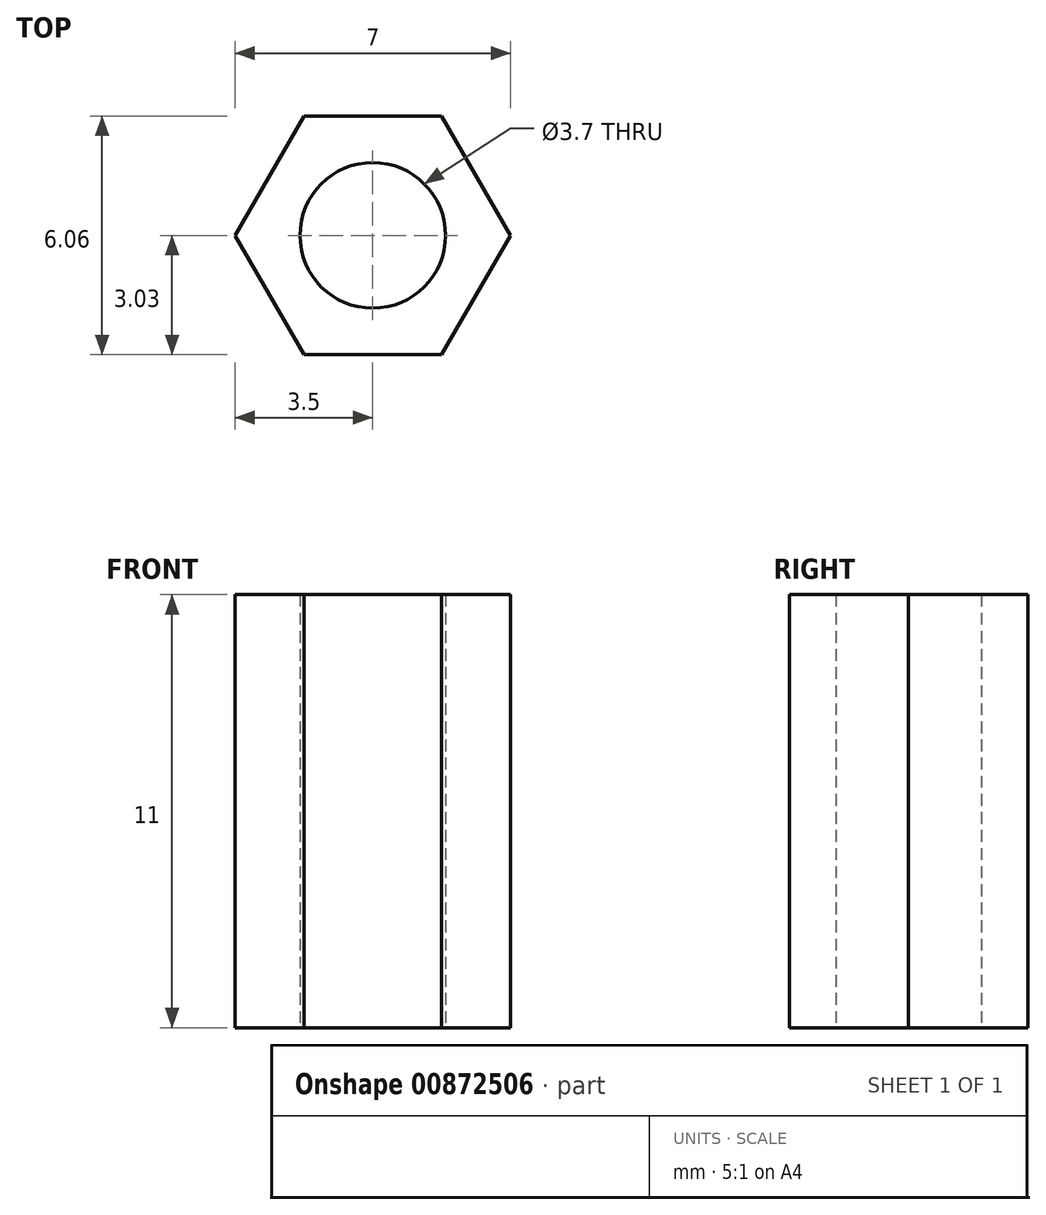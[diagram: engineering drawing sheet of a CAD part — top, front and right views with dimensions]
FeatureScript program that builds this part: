
annotation { "Feature Type Name" : "Feature", "Feature Type Description" : "" }
export const myFeature = defineFeature(function(context is Context, id is Id, definition is map)
    precondition{}
    {
        {
            var Q0;
            Q0=qCreatedBy(makeId("Top.planeOp"),FACE);
            var sketch = newSketch(context, id + "F0", { "sketchPlane" : qUnion([Q0])});
            skCircle(sketch, "E0", {"center": v(0, 0) * mm, "radius": 1.85 * mm});
            skCircle(sketch, "E1.cCircle", {"center": v(0, 0) * mm, "radius": 3.5 * mm, "construction": true});
            skLineSegment(sketch, "E1.0", {"start": v(3.5, 0) * mm, "end": v(1.75, -3.03) * mm});
            skLineSegment(sketch, "E1.1", {"start": v(1.75, -3.03) * mm, "end": v(-1.75, -3.03) * mm});
            skLineSegment(sketch, "E1.2", {"start": v(-1.75, -3.03) * mm, "end": v(-3.5, 0) * mm});
            skLineSegment(sketch, "E1.3", {"start": v(-3.5, 0) * mm, "end": v(-1.75, 3.03) * mm});
            skLineSegment(sketch, "E1.4", {"start": v(-1.75, 3.03) * mm, "end": v(1.75, 3.03) * mm});
            skLineSegment(sketch, "E1.5", {"start": v(1.75, 3.03) * mm, "end": v(3.5, 0) * mm});
            skSolve(sketch);
        }
        {
            var Q0;
            Q0=makeQuery(id+"F0.imprint","IMPRINT",FACE,{"disambiguationData":[TD([[makeQuery(id+"F0.imprint","IMPRINT",EDGE,{"derivedFrom":sQuery(id+"F0.wireOp",EDGE,"E0")}),-1.0]])]});
            extrude(context, id + "F1", {"entities" : qUnion([Q0]), "depth" : 11 * mm, "offsetDistance" : 25 * mm});
        }
    });
